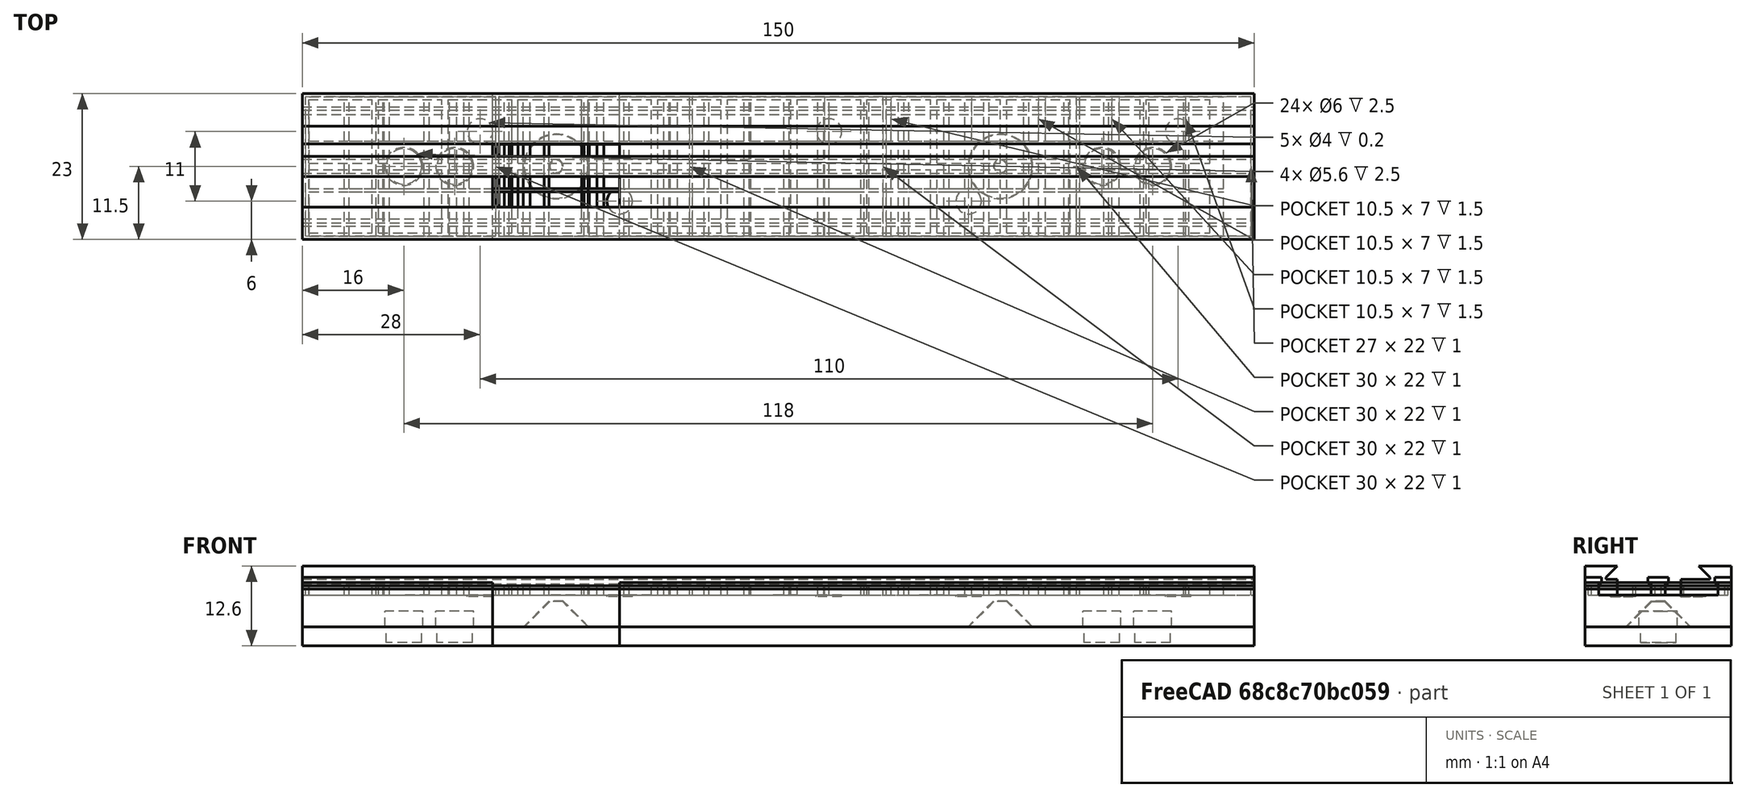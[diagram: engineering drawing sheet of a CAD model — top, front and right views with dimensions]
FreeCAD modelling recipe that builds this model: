
FCSTD DOCUMENT  (FreeCAD 0.19R24366 (Git))
Label: SMD_TRAY_02
License: All rights reserved
LicenseURL: http://en.wikipedia.org/wiki/All_rights_reserved
objects: Part::Box×87, Part::MultiFuse×60, Part::Cylinder×20, Part::Cut×13, Part::Feature×6, Part::Cone×4
note: 190 computed .brp shape members not serialized (recipe doc carries the construction recipe); baked Part::Feature solids carry a one-line shape summary decoded from their .brp

FEATURE [Part::Cone] Cone  label="cone_001"
  Angle = 360
  AttacherType = Attacher::AttachEngine3D
  Height = 4
  Placement = pos=(40,11.5,3) rot=(0,0,1;0rad)
  Radius1 = 5
  Radius2 = 1
FEATURE [Part::Box] Box  label="base"
  AttacherType = Attacher::AttachEngine3D
  Height = 3
  Length = 150
  Width = 23
FEATURE [Part::Cylinder] Cylinder  label="magnet_001"
  Angle = 360
  AttacherType = Attacher::AttachEngine3D
  Height = 2.5
  Placement = pos=(16,11.5,0.5) rot=(0,0,1;0rad)
  Radius = 2.8
FEATURE [Part::Cylinder] Cylinder001  label="magnet_002"
  Angle = 360
  AttacherType = Attacher::AttachEngine3D
  Height = 2.5
  Placement = pos=(24,11.5,0.5) rot=(0,0,1;0rad)
  Radius = 2.8
FEATURE [Part::Cylinder] Cylinder002  label="magnet_003"
  Angle = 360
  AttacherType = Attacher::AttachEngine3D
  Height = 2.5
  Placement = pos=(126,11.5,0.5) rot=(0,0,1;0rad)
  Radius = 2.8
FEATURE [Part::Cylinder] Cylinder003  label="magnet_004"
  Angle = 360
  AttacherType = Attacher::AttachEngine3D
  Height = 2.5
  Placement = pos=(134,11.5,0.5) rot=(0,0,1;0rad)
  Radius = 2.8
FEATURE [Part::Cone] Cone001  label="cone_002"
  Angle = 360
  AttacherType = Attacher::AttachEngine3D
  Height = 4
  Placement = pos=(110,11.5,3) rot=(0,0,1;0rad)
  Radius1 = 5
  Radius2 = 1
FEATURE [Part::MultiFuse] Fusion
  Shapes = -> [Cylinder,Cylinder002,Cylinder001,Cylinder003]
FEATURE [Part::MultiFuse] Fusion001
  Shapes = -> [Cone001,Cone,Box]
FEATURE [Part::Cut] Cut  label="BOTTOM"
  Base = -> Fusion001
  Tool = -> Fusion
FEATURE [Part::Box] Box001  label="Cube"
  AttacherType = Attacher::AttachEngine3D
  Height = 5
  Length = 150
  Placement = pos=(0,0,3) rot=(0,0,1;0rad)
  Width = 23
FEATURE [Part::Cone] Cone002  label="cone_003"
  Angle = 360
  AttacherType = Attacher::AttachEngine3D
  Height = 4.1
  Placement = pos=(40,11.5,3) rot=(0,0,1;0rad)
  Radius1 = 5.1
  Radius2 = 1.1
FEATURE [Part::Cone] Cone003  label="cone_004"
  Angle = 360
  AttacherType = Attacher::AttachEngine3D
  Height = 4.1
  Placement = pos=(110,11.5,3) rot=(0,0,1;0rad)
  Radius1 = 5.1
  Radius2 = 1.1
FEATURE [Part::Cylinder] Cylinder004  label="magnet_005"
  Angle = 360
  AttacherType = Attacher::AttachEngine3D
  Height = 2.5
  Placement = pos=(16,11.5,3) rot=(0,0,1;0rad)
  Radius = 3
FEATURE [Part::Cylinder] Cylinder005  label="magnet_006"
  Angle = 360
  AttacherType = Attacher::AttachEngine3D
  Height = 2.5
  Placement = pos=(126,11.5,3) rot=(0,0,1;0rad)
  Radius = 3
FEATURE [Part::Cylinder] Cylinder006  label="magnet_007"
  Angle = 360
  AttacherType = Attacher::AttachEngine3D
  Height = 2.5
  Placement = pos=(24,11.5,3) rot=(0,0,1;0rad)
  Radius = 3
FEATURE [Part::Cylinder] Cylinder007  label="magnet_008"
  Angle = 360
  AttacherType = Attacher::AttachEngine3D
  Height = 2.5
  Placement = pos=(134,11.5,3) rot=(0,0,1;0rad)
  Radius = 3
FEATURE [Part::MultiFuse] Fusion002  label="removals"
  Shapes = -> [Cylinder004,Cone002,Cone003,Cylinder006,Cylinder005,Cylinder007]
FEATURE [Part::Cut] Cut001  label="TOP"
  Base = -> Box001
  Tool = -> Fusion002
FEATURE [Part::Box] Box014  label="Base002"
  AttacherType = Attacher::AttachEngine3D
  Height = 2.8
  Length = 150
  Placement = pos=(0,0,9) rot=(0,0,1;0rad)
  Width = 23
FEATURE [Part::Box] Box015  label="tape_01"
  AttacherType = Attacher::AttachEngine3D
  Height = 1.8
  Length = 150
  Placement = pos=(0,2.1,9) rot=(0,0,1;0rad)
  Width = 8.3
FEATURE [Part::Box] Box016  label="tape_002"
  AttacherType = Attacher::AttachEngine3D
  Height = 1.8
  Length = 150
  Placement = pos=(0,12.6,9) rot=(0,0,1;0rad)
  Width = 8.3
FEATURE [Part::Box] Box017  label="tape_003"
  AttacherType = Attacher::AttachEngine3D
  Height = 1
  Length = 150
  Placement = pos=(0,2.6,10.8) rot=(0,0,1;0rad)
  Width = 7.3
FEATURE [Part::Box] Box018  label="tape_004"
  AttacherType = Attacher::AttachEngine3D
  Height = 1
  Length = 150
  Placement = pos=(0,13.1,10.8) rot=(0,0,1;0rad)
  Width = 7.3
FEATURE [Part::MultiFuse] Fusion006
  Shapes = -> [Box015,Box017,Box018,Box016]
FEATURE [Part::Cut] Cut006  label="2X_8mm_tape"
  Base = -> Box014
  Placement = pos=(0,0,-1) rot=(0,0,1;0rad)
  Tool = -> Fusion006
FEATURE [Part::Box] Box019  label="deletor_001"
  AttacherType = Attacher::AttachEngine3D
  Height = 10
  Length = 30
  Width = 23
FEATURE [Part::Box] Box020  label="deletor_002"
  AttacherType = Attacher::AttachEngine3D
  Height = 10
  Length = 100
  Placement = pos=(50,0,0) rot=(0,0,1;0rad)
  Width = 23
FEATURE [Part::MultiFuse] Fusion007  label="del_001"
  Shapes = -> [Box019,Box020]
FEATURE [Part::MultiFuse] Fusion008  label="del_002"
  Shapes = -> [Box019,Box020]
FEATURE [Part::MultiFuse] Fusion009  label="TOP_2X_8mm"
  Shapes = -> [Cut001,Cut006]
FEATURE [Part::Cut] Cut007  label="TOP001"
  Base = -> Box001
  Tool = -> Fusion002
FEATURE [Part::Box] Box021  label="Base003"
  AttacherType = Attacher::AttachEngine3D
  Height = 1.5
  Length = 150
  Placement = pos=(0,0,8) rot=(0,0,1;0rad)
  Width = 23
FEATURE [Part::Box] Box022  label="Cube001"
  AttacherType = Attacher::AttachEngine3D
  Height = 1.5
  Length = 5.5
  Placement = pos=(1.1,0.5,8) rot=(0,0,1;0rad)
  Width = 7
FEATURE [Part::Box] Box023  label="Cube002"
  AttacherType = Attacher::AttachEngine3D
  Height = 1.5
  Length = 5.5
  Placement = pos=(1.1,8,8) rot=(0,0,1;0rad)
  Width = 7
FEATURE [Part::Box] Box024  label="Cube003"
  AttacherType = Attacher::AttachEngine3D
  Height = 1.5
  Length = 5.5
  Placement = pos=(1.1,15.5,8) rot=(0,0,1;0rad)
  Width = 7
FEATURE [Part::MultiFuse] Fusion010  label="row_000"
  Shapes = -> [Box022,Box024,Box023]
FEATURE [Part::MultiFuse] Fusion011  label="row_001"
  Placement = pos=(6.3,0,0) rot=(0,0,1;0rad)
  Shapes = -> [Box022,Box024,Box023]
FEATURE [Part::MultiFuse] Fusion012  label="row_002"
  Placement = pos=(12.6,0,0) rot=(0,0,1;0rad)
  Shapes = -> [Box022,Box024,Box023]
FEATURE [Part::MultiFuse] Fusion013  label="row_003"
  Placement = pos=(18.9,0,0) rot=(0,0,1;0rad)
  Shapes = -> [Box022,Box024,Box023]
FEATURE [Part::MultiFuse] Fusion014  label="row_004"
  Placement = pos=(25.2,0,0) rot=(0,0,1;0rad)
  Shapes = -> [Box022,Box024,Box023]
FEATURE [Part::MultiFuse] Fusion015  label="row_005"
  Placement = pos=(31.5,0,0) rot=(0,0,1;0rad)
  Shapes = -> [Box022,Box024,Box023]
FEATURE [Part::MultiFuse] Fusion016  label="row_006"
  Placement = pos=(37.8,0,0) rot=(0,0,1;0rad)
  Shapes = -> [Box022,Box024,Box023]
FEATURE [Part::MultiFuse] Fusion017  label="row_007"
  Placement = pos=(44.1,0,0) rot=(0,0,1;0rad)
  Shapes = -> [Box022,Box024,Box023]
FEATURE [Part::MultiFuse] Fusion018  label="row_008"
  Placement = pos=(50.4,0,0) rot=(0,0,1;0rad)
  Shapes = -> [Box022,Box024,Box023]
FEATURE [Part::MultiFuse] Fusion019  label="row_009"
  Placement = pos=(56.7,0,0) rot=(0,0,1;0rad)
  Shapes = -> [Box022,Box024,Box023]
FEATURE [Part::MultiFuse] Fusion020  label="10 of them"
  Shapes = -> [Fusion010,Fusion019,Fusion018,Fusion014,Fusion015,Fusion017,Fusion016,Fusion013,Fusion011,Fusion012]
FEATURE [Part::MultiFuse] Fusion021  label="10 of them001"
  Placement = pos=(63,0,0) rot=(0,0,1;0rad)
  Shapes = -> [Fusion010,Fusion019,Fusion018,Fusion014,Fusion015,Fusion017,Fusion016,Fusion013,Fusion011,Fusion012]
FEATURE [Part::MultiFuse] Fusion022  label="row_010"
  Placement = pos=(126,0,0) rot=(0,0,1;0rad)
  Shapes = -> [Box022,Box024,Box023]
FEATURE [Part::MultiFuse] Fusion023  label="row_011"
  Placement = pos=(132.3,0,0) rot=(0,0,1;0rad)
  Shapes = -> [Box022,Box024,Box023]
FEATURE [Part::MultiFuse] Fusion024  label="row_012"
  Placement = pos=(138.6,0,0) rot=(0,0,1;0rad)
  Shapes = -> [Box022,Box024,Box023]
FEATURE [Part::MultiFuse] Fusion025  label="Holes_SOIC8"
  Shapes = -> [Fusion020,Fusion021,Fusion022,Fusion024,Fusion023]
FEATURE [Part::Cut] Cut008  label="69X_SOIC8"
  Base = -> Box021
  Tool = -> Fusion025
FEATURE [Part::MultiFuse] Fusion026  label="TOP_69X_SOIC8"
  Shapes = -> [Cut007,Cut008]
FEATURE [Part::Cut] Cut009  label="TOP002"
  Base = -> Box001
  Tool = -> Fusion002
FEATURE [Part::Box] Box025  label="Base004"
  AttacherType = Attacher::AttachEngine3D
  Height = 1
  Length = 150
  Placement = pos=(0,0,8) rot=(0,0,1;0rad)
  Width = 23
FEATURE [Part::Box] Box026  label="Cube004"
  AttacherType = Attacher::AttachEngine3D
  Height = 1.5
  Length = 30
  Placement = pos=(0.5,0.5,8) rot=(0,0,1;0rad)
  Width = 22
FEATURE [Part::Box] Box027  label="Cube005"
  AttacherType = Attacher::AttachEngine3D
  Height = 1.5
  Length = 30
  Placement = pos=(31,0.5,8) rot=(0,0,1;0rad)
  Width = 22
FEATURE [Part::Box] Box028  label="Cube006"
  AttacherType = Attacher::AttachEngine3D
  Height = 1.5
  Length = 30
  Placement = pos=(61.5,0.5,8) rot=(0,0,1;0rad)
  Width = 22
FEATURE [Part::Box] Box029  label="Cube007"
  AttacherType = Attacher::AttachEngine3D
  Height = 1.5
  Length = 30
  Placement = pos=(92,0.5,8) rot=(0,0,1;0rad)
  Width = 22
FEATURE [Part::Box] Box030  label="Cube008"
  AttacherType = Attacher::AttachEngine3D
  Height = 1.5
  Length = 27
  Placement = pos=(122.5,0.5,8) rot=(0,0,1;0rad)
  Width = 22
FEATURE [Part::MultiFuse] Fusion027  label="remove_holes"
  Shapes = -> [Box026,Box029,Box030,Box028,Box027]
FEATURE [Part::Cut] Cut010  label="5x_loose"
  Base = -> Box025
  Tool = -> Fusion027
FEATURE [Part::MultiFuse] Fusion028  label="TOP_5X_Loose"
  Shapes = -> [Cut009,Cut010]
FEATURE [Part::Feature] Cut007001  label="TOP003"
  shape: bbox 150 x 23 x 5 mm, 18 faces (baked)
FEATURE [Part::Feature] Box021001  label="Base005"
  Placement = pos=(0,0,8) rot=(0,0,1;0rad)
  shape: bbox 150 x 23 x 1.5 mm, 6 faces (baked)
FEATURE [Part::Box] Box021002  label="Cube009"
  AttacherType = Attacher::AttachEngine3D
  Height = 1.5
  Length = 10.5
  Placement = pos=(1.1,0.5,8) rot=(0,0,1;0rad)
  Width = 7
FEATURE [Part::Box] Box021003  label="Cube010"
  AttacherType = Attacher::AttachEngine3D
  Height = 1.5
  Length = 10.5
  Placement = pos=(1.1,8,8) rot=(0,0,1;0rad)
  Width = 7
FEATURE [Part::Box] Box021004  label="Cube011"
  AttacherType = Attacher::AttachEngine3D
  Height = 1.5
  Length = 10.5
  Placement = pos=(1.1,15.5,8) rot=(0,0,1;0rad)
  Width = 7
FEATURE [Part::MultiFuse] Fusion029  label="row__01"
  Shapes = -> [Box021002,Box021003,Box021004]
FEATURE [Part::Box] Box021005  label="Cube012"
  AttacherType = Attacher::AttachEngine3D
  Height = 1.5
  Length = 10.5
  Placement = pos=(1.1,8,8) rot=(0,0,1;0rad)
  Width = 7
FEATURE [Part::Box] Box021006  label="Cube013"
  AttacherType = Attacher::AttachEngine3D
  Height = 1.5
  Length = 10.5
  Placement = pos=(1.1,15.5,8) rot=(0,0,1;0rad)
  Width = 7
FEATURE [Part::Box] Box021007  label="Cube014"
  AttacherType = Attacher::AttachEngine3D
  Height = 1.5
  Length = 10.5
  Placement = pos=(1.1,0.5,8) rot=(0,0,1;0rad)
  Width = 7
FEATURE [Part::MultiFuse] Fusion030  label="row__002"
  Placement = pos=(11.6,0,0) rot=(0,0,1;0rad)
  Shapes = -> [Box021007,Box021005,Box021006]
FEATURE [Part::Box] Box021008  label="Cube015"
  AttacherType = Attacher::AttachEngine3D
  Height = 1.5
  Length = 10.5
  Placement = pos=(1.1,0.5,8) rot=(0,0,1;0rad)
  Width = 7
FEATURE [Part::Box] Box021009  label="Cube016"
  AttacherType = Attacher::AttachEngine3D
  Height = 1.5
  Length = 10.5
  Placement = pos=(1.1,8,8) rot=(0,0,1;0rad)
  Width = 7
FEATURE [Part::Box] Box021010  label="Cube017"
  AttacherType = Attacher::AttachEngine3D
  Height = 1.5
  Length = 10.5
  Placement = pos=(1.1,15.5,8) rot=(0,0,1;0rad)
  Width = 7
FEATURE [Part::MultiFuse] Fusion031  label="row__003"
  Placement = pos=(23.2,0,0) rot=(0,0,1;0rad)
  Shapes = -> [Box021008,Box021009,Box021010]
FEATURE [Part::Box] Box021011  label="Cube018"
  AttacherType = Attacher::AttachEngine3D
  Height = 1.5
  Length = 10.5
  Placement = pos=(1.1,0.5,8) rot=(0,0,1;0rad)
  Width = 7
FEATURE [Part::Box] Box021012  label="Cube019"
  AttacherType = Attacher::AttachEngine3D
  Height = 1.5
  Length = 10.5
  Placement = pos=(1.1,8,8) rot=(0,0,1;0rad)
  Width = 7
FEATURE [Part::Box] Box021013  label="Cube020"
  AttacherType = Attacher::AttachEngine3D
  Height = 1.5
  Length = 10.5
  Placement = pos=(1.1,15.5,8) rot=(0,0,1;0rad)
  Width = 7
FEATURE [Part::MultiFuse] Fusion032  label="row__004"
  Placement = pos=(34.8,0,0) rot=(0,0,1;0rad)
  Shapes = -> [Box021011,Box021012,Box021013]
FEATURE [Part::Box] Box021014  label="Cube021"
  AttacherType = Attacher::AttachEngine3D
  Height = 1.5
  Length = 10.5
  Placement = pos=(1.1,0.5,8) rot=(0,0,1;0rad)
  Width = 7
FEATURE [Part::Box] Box021015  label="Cube022"
  AttacherType = Attacher::AttachEngine3D
  Height = 1.5
  Length = 10.5
  Placement = pos=(1.1,8,8) rot=(0,0,1;0rad)
  Width = 7
FEATURE [Part::Box] Box021016  label="Cube023"
  AttacherType = Attacher::AttachEngine3D
  Height = 1.5
  Length = 10.5
  Placement = pos=(1.1,15.5,8) rot=(0,0,1;0rad)
  Width = 7
FEATURE [Part::MultiFuse] Fusion033  label="row__005"
  Placement = pos=(46.4,0,0) rot=(0,0,1;0rad)
  Shapes = -> [Box021014,Box021015,Box021016]
FEATURE [Part::Box] Box021017  label="Cube024"
  AttacherType = Attacher::AttachEngine3D
  Height = 1.5
  Length = 10.5
  Placement = pos=(1.1,0.5,8) rot=(0,0,1;0rad)
  Width = 7
FEATURE [Part::Box] Box021018  label="Cube025"
  AttacherType = Attacher::AttachEngine3D
  Height = 1.5
  Length = 10.5
  Placement = pos=(1.1,8,8) rot=(0,0,1;0rad)
  Width = 7
FEATURE [Part::Box] Box021019  label="Cube026"
  AttacherType = Attacher::AttachEngine3D
  Height = 1.5
  Length = 10.5
  Placement = pos=(1.1,15.5,8) rot=(0,0,1;0rad)
  Width = 7
FEATURE [Part::MultiFuse] Fusion034  label="row__006"
  Placement = pos=(58,0,0) rot=(0,0,1;0rad)
  Shapes = -> [Box021017,Box021018,Box021019]
FEATURE [Part::Box] Box021020  label="Cube027"
  AttacherType = Attacher::AttachEngine3D
  Height = 1.5
  Length = 10.5
  Placement = pos=(1.1,0.5,8) rot=(0,0,1;0rad)
  Width = 7
FEATURE [Part::Box] Box021021  label="Cube028"
  AttacherType = Attacher::AttachEngine3D
  Height = 1.5
  Length = 10.5
  Placement = pos=(1.1,8,8) rot=(0,0,1;0rad)
  Width = 7
FEATURE [Part::Box] Box021022  label="Cube029"
  AttacherType = Attacher::AttachEngine3D
  Height = 1.5
  Length = 10.5
  Placement = pos=(1.1,15.5,8) rot=(0,0,1;0rad)
  Width = 7
FEATURE [Part::MultiFuse] Fusion035  label="row__007"
  Placement = pos=(69.6,0,0) rot=(0,0,1;0rad)
  Shapes = -> [Box021020,Box021021,Box021022]
FEATURE [Part::Box] Box021023  label="Cube030"
  AttacherType = Attacher::AttachEngine3D
  Height = 1.5
  Length = 10.5
  Placement = pos=(1.1,0.5,8) rot=(0,0,1;0rad)
  Width = 7
FEATURE [Part::Box] Box021024  label="Cube031"
  AttacherType = Attacher::AttachEngine3D
  Height = 1.5
  Length = 10.5
  Placement = pos=(1.1,8,8) rot=(0,0,1;0rad)
  Width = 7
FEATURE [Part::Box] Box021025  label="Cube032"
  AttacherType = Attacher::AttachEngine3D
  Height = 1.5
  Length = 10.5
  Placement = pos=(1.1,15.5,8) rot=(0,0,1;0rad)
  Width = 7
FEATURE [Part::MultiFuse] Fusion036  label="row__008"
  Placement = pos=(81.2,0,0) rot=(0,0,1;0rad)
  Shapes = -> [Box021023,Box021024,Box021025]
FEATURE [Part::Box] Box021026  label="Cube033"
  AttacherType = Attacher::AttachEngine3D
  Height = 1.5
  Length = 10.5
  Placement = pos=(1.1,0.5,8) rot=(0,0,1;0rad)
  Width = 7
FEATURE [Part::Box] Box021027  label="Cube034"
  AttacherType = Attacher::AttachEngine3D
  Height = 1.5
  Length = 10.5
  Placement = pos=(1.1,8,8) rot=(0,0,1;0rad)
  Width = 7
FEATURE [Part::Box] Box021028  label="Cube035"
  AttacherType = Attacher::AttachEngine3D
  Height = 1.5
  Length = 10.5
  Placement = pos=(1.1,15.5,8) rot=(0,0,1;0rad)
  Width = 7
FEATURE [Part::MultiFuse] Fusion037  label="row__009"
  Placement = pos=(92.8,0,0) rot=(0,0,1;0rad)
  Shapes = -> [Box021026,Box021027,Box021028]
FEATURE [Part::Box] Box021029  label="Cube036"
  AttacherType = Attacher::AttachEngine3D
  Height = 1.5
  Length = 10.5
  Placement = pos=(1.1,0.5,8) rot=(0,0,1;0rad)
  Width = 7
FEATURE [Part::Box] Box021030  label="Cube037"
  AttacherType = Attacher::AttachEngine3D
  Height = 1.5
  Length = 10.5
  Placement = pos=(1.1,8,8) rot=(0,0,1;0rad)
  Width = 7
FEATURE [Part::Box] Box021031  label="Cube038"
  AttacherType = Attacher::AttachEngine3D
  Height = 1.5
  Length = 10.5
  Placement = pos=(1.1,15.5,8) rot=(0,0,1;0rad)
  Width = 7
FEATURE [Part::MultiFuse] Fusion038  label="row__010"
  Placement = pos=(104.4,0,0) rot=(0,0,1;0rad)
  Shapes = -> [Box021029,Box021030,Box021031]
FEATURE [Part::Box] Box021032  label="Cube039"
  AttacherType = Attacher::AttachEngine3D
  Height = 1.5
  Length = 10.5
  Placement = pos=(1.1,0.5,8) rot=(0,0,1;0rad)
  Width = 7
FEATURE [Part::Box] Box021033  label="Cube040"
  AttacherType = Attacher::AttachEngine3D
  Height = 1.5
  Length = 10.5
  Placement = pos=(1.1,8,8) rot=(0,0,1;0rad)
  Width = 7
FEATURE [Part::Box] Box021034  label="Cube041"
  AttacherType = Attacher::AttachEngine3D
  Height = 1.5
  Length = 10.5
  Placement = pos=(1.1,15.5,8) rot=(0,0,1;0rad)
  Width = 7
FEATURE [Part::MultiFuse] Fusion039  label="row__011"
  Placement = pos=(116,0,0) rot=(0,0,1;0rad)
  Shapes = -> [Box021032,Box021033,Box021034]
FEATURE [Part::Box] Box021035  label="Cube042"
  AttacherType = Attacher::AttachEngine3D
  Height = 1.5
  Length = 10.5
  Placement = pos=(1.1,0.5,8) rot=(0,0,1;0rad)
  Width = 7
FEATURE [Part::Box] Box021036  label="Cube043"
  AttacherType = Attacher::AttachEngine3D
  Height = 1.5
  Length = 10.5
  Placement = pos=(1.1,8,8) rot=(0,0,1;0rad)
  Width = 7
FEATURE [Part::Box] Box021037  label="Cube044"
  AttacherType = Attacher::AttachEngine3D
  Height = 1.5
  Length = 10.5
  Placement = pos=(1.1,15.5,8) rot=(0,0,1;0rad)
  Width = 7
FEATURE [Part::MultiFuse] Fusion040  label="row__012"
  Placement = pos=(127.6,0,0) rot=(0,0,1;0rad)
  Shapes = -> [Box021035,Box021036,Box021037]
FEATURE [Part::Cylinder] Cylinder008  label="mark_5"
  Angle = 360
  AttacherType = Attacher::AttachEngine3D
  Height = 0.2
  Placement = pos=(18,12,8) rot=(0,0,1;0rad)
  Radius = 2
FEATURE [Part::Cylinder] Cylinder009  label="mark_10"
  Angle = 360
  AttacherType = Attacher::AttachEngine3D
  Height = 0.2
  Placement = pos=(41,19,8) rot=(0,0,1;0rad)
  Radius = 2
FEATURE [Part::Cylinder] Cylinder010  label="mark_15"
  Angle = 360
  AttacherType = Attacher::AttachEngine3D
  Height = 0.2
  Placement = pos=(53,4,8) rot=(0,0,1;0rad)
  Radius = 2
FEATURE [Part::Cylinder] Cylinder011  label="mark_20"
  Angle = 360
  AttacherType = Attacher::AttachEngine3D
  Height = 0.2
  Placement = pos=(76,12,8) rot=(0,0,1;0rad)
  Radius = 2
FEATURE [Part::Cylinder] Cylinder012  label="mark_25"
  Angle = 360
  AttacherType = Attacher::AttachEngine3D
  Height = 0.2
  Placement = pos=(99,19,8) rot=(0,0,1;0rad)
  Radius = 2
FEATURE [Part::Cylinder] Cylinder013  label="mark_30"
  Angle = 360
  AttacherType = Attacher::AttachEngine3D
  Height = 0.2
  Placement = pos=(111,4,8) rot=(0,0,1;0rad)
  Radius = 2
FEATURE [Part::Cylinder] Cylinder014  label="mark_35"
  Angle = 360
  AttacherType = Attacher::AttachEngine3D
  Height = 0.2
  Placement = pos=(134,12,8) rot=(0,0,1;0rad)
  Radius = 2
FEATURE [Part::MultiFuse] Fusion041
  Shapes = -> [Fusion029,Fusion030,Fusion031,Fusion032,Fusion033,Fusion034,Fusion035,Fusion036,Fusion037,Fusion038,Fusion039,Fusion040]
FEATURE [Part::MultiFuse] Fusion042
  Shapes = -> [Cylinder008,Cylinder009,Cylinder010,Cylinder011,Cylinder012,Cylinder013,Cylinder014]
FEATURE [Part::MultiFuse] Fusion043
  Shapes = -> [Cut007001,Box021001]
FEATURE [Part::Cut] Cut007002
  Base = -> Fusion043
  Tool = -> Fusion042
FEATURE [Part::Cut] Cut007003  label="TOP_36X_SOIC16"
  Base = -> Cut007002
  Tool = -> Fusion041
FEATURE [Part::Feature] Box021038  label="Base006"
  Placement = pos=(0,0,8) rot=(0,0,1;0rad)
  shape: bbox 150 x 23 x 1.5 mm, 6 faces (baked)
FEATURE [Part::Feature] Cut007004  label="TOP004"
  shape: bbox 150 x 23 x 5 mm, 18 faces (baked)
FEATURE [Part::Box] Box021039  label="Cube045"
  AttacherType = Attacher::AttachEngine3D
  Height = 1.5
  Length = 10
  Placement = pos=(1,1,8) rot=(0,0,1;0rad)
  Width = 10
FEATURE [Part::Box] Box021040  label="Cube046"
  AttacherType = Attacher::AttachEngine3D
  Height = 1.5
  Length = 10
  Placement = pos=(1,12,8) rot=(0,0,1;0rad)
  Width = 10
FEATURE [Part::MultiFuse] Fusion044
  Shapes = -> [Box021039,Box021040]
FEATURE [Part::Box] Box021041  label="Cube047"
  AttacherType = Attacher::AttachEngine3D
  Height = 1.5
  Length = 10
  Placement = pos=(1,12,8) rot=(0,0,1;0rad)
  Width = 10
FEATURE [Part::Box] Box021042  label="Cube048"
  AttacherType = Attacher::AttachEngine3D
  Height = 1.5
  Length = 10
  Placement = pos=(1,1,8) rot=(0,0,1;0rad)
  Width = 10
FEATURE [Part::MultiFuse] Fusion045
  Placement = pos=(11,0,0) rot=(0,0,1;0rad)
  Shapes = -> [Box021042,Box021041]
FEATURE [Part::Box] Box021043  label="Cube049"
  AttacherType = Attacher::AttachEngine3D
  Height = 1.5
  Length = 10
  Placement = pos=(1,12,8) rot=(0,0,1;0rad)
  Width = 10
FEATURE [Part::Box] Box021044  label="Cube050"
  AttacherType = Attacher::AttachEngine3D
  Height = 1.5
  Length = 10
  Placement = pos=(1,1,8) rot=(0,0,1;0rad)
  Width = 10
FEATURE [Part::MultiFuse] Fusion046
  Placement = pos=(22,0,0) rot=(0,0,1;0rad)
  Shapes = -> [Box021044,Box021043]
FEATURE [Part::Box] Box021045  label="Cube051"
  AttacherType = Attacher::AttachEngine3D
  Height = 1.5
  Length = 10
  Placement = pos=(1,12,8) rot=(0,0,1;0rad)
  Width = 10
FEATURE [Part::Box] Box021046  label="Cube052"
  AttacherType = Attacher::AttachEngine3D
  Height = 1.5
  Length = 10
  Placement = pos=(1,1,8) rot=(0,0,1;0rad)
  Width = 10
FEATURE [Part::MultiFuse] Fusion047
  Placement = pos=(33,0,0) rot=(0,0,1;0rad)
  Shapes = -> [Box021046,Box021045]
FEATURE [Part::Box] Box021047  label="Cube053"
  AttacherType = Attacher::AttachEngine3D
  Height = 1.5
  Length = 10
  Placement = pos=(1,12,8) rot=(0,0,1;0rad)
  Width = 10
FEATURE [Part::Box] Box021048  label="Cube054"
  AttacherType = Attacher::AttachEngine3D
  Height = 1.5
  Length = 10
  Placement = pos=(1,1,8) rot=(0,0,1;0rad)
  Width = 10
FEATURE [Part::MultiFuse] Fusion048
  Placement = pos=(44,0,0) rot=(0,0,1;0rad)
  Shapes = -> [Box021048,Box021047]
FEATURE [Part::Box] Box021049  label="Cube055"
  AttacherType = Attacher::AttachEngine3D
  Height = 1.5
  Length = 10
  Placement = pos=(1,12,8) rot=(0,0,1;0rad)
  Width = 10
FEATURE [Part::Box] Box021050  label="Cube056"
  AttacherType = Attacher::AttachEngine3D
  Height = 1.5
  Length = 10
  Placement = pos=(1,1,8) rot=(0,0,1;0rad)
  Width = 10
FEATURE [Part::MultiFuse] Fusion049
  Placement = pos=(55,0,0) rot=(0,0,1;0rad)
  Shapes = -> [Box021050,Box021049]
FEATURE [Part::Box] Box021051  label="Cube057"
  AttacherType = Attacher::AttachEngine3D
  Height = 1.5
  Length = 10
  Placement = pos=(1,12,8) rot=(0,0,1;0rad)
  Width = 10
FEATURE [Part::Box] Box021052  label="Cube058"
  AttacherType = Attacher::AttachEngine3D
  Height = 1.5
  Length = 10
  Placement = pos=(1,1,8) rot=(0,0,1;0rad)
  Width = 10
FEATURE [Part::MultiFuse] Fusion050
  Placement = pos=(66,0,0) rot=(0,0,1;0rad)
  Shapes = -> [Box021052,Box021051]
FEATURE [Part::Box] Box021053  label="Cube059"
  AttacherType = Attacher::AttachEngine3D
  Height = 1.5
  Length = 10
  Placement = pos=(1,12,8) rot=(0,0,1;0rad)
  Width = 10
FEATURE [Part::Box] Box021054  label="Cube060"
  AttacherType = Attacher::AttachEngine3D
  Height = 1.5
  Length = 10
  Placement = pos=(1,1,8) rot=(0,0,1;0rad)
  Width = 10
FEATURE [Part::MultiFuse] Fusion051
  Placement = pos=(77,0,0) rot=(0,0,1;0rad)
  Shapes = -> [Box021054,Box021053]
FEATURE [Part::Box] Box021055  label="Cube061"
  AttacherType = Attacher::AttachEngine3D
  Height = 1.5
  Length = 10
  Placement = pos=(1,12,8) rot=(0,0,1;0rad)
  Width = 10
FEATURE [Part::Box] Box021056  label="Cube062"
  AttacherType = Attacher::AttachEngine3D
  Height = 1.5
  Length = 10
  Placement = pos=(1,1,8) rot=(0,0,1;0rad)
  Width = 10
FEATURE [Part::MultiFuse] Fusion052
  Placement = pos=(88,0,0) rot=(0,0,1;0rad)
  Shapes = -> [Box021056,Box021055]
FEATURE [Part::Box] Box021057  label="Cube063"
  AttacherType = Attacher::AttachEngine3D
  Height = 1.5
  Length = 10
  Placement = pos=(1,12,8) rot=(0,0,1;0rad)
  Width = 10
FEATURE [Part::Box] Box021058  label="Cube064"
  AttacherType = Attacher::AttachEngine3D
  Height = 1.5
  Length = 10
  Placement = pos=(1,1,8) rot=(0,0,1;0rad)
  Width = 10
FEATURE [Part::MultiFuse] Fusion053
  Placement = pos=(99,0,0) rot=(0,0,1;0rad)
  Shapes = -> [Box021058,Box021057]
FEATURE [Part::Box] Box021059  label="Cube065"
  AttacherType = Attacher::AttachEngine3D
  Height = 1.5
  Length = 10
  Placement = pos=(1,12,8) rot=(0,0,1;0rad)
  Width = 10
FEATURE [Part::Box] Box021060  label="Cube066"
  AttacherType = Attacher::AttachEngine3D
  Height = 1.5
  Length = 10
  Placement = pos=(1,1,8) rot=(0,0,1;0rad)
  Width = 10
FEATURE [Part::MultiFuse] Fusion054
  Placement = pos=(110,0,0) rot=(0,0,1;0rad)
  Shapes = -> [Box021060,Box021059]
FEATURE [Part::Box] Box021061  label="Cube067"
  AttacherType = Attacher::AttachEngine3D
  Height = 1.5
  Length = 10
  Placement = pos=(1,12,8) rot=(0,0,1;0rad)
  Width = 10
FEATURE [Part::Box] Box021062  label="Cube068"
  AttacherType = Attacher::AttachEngine3D
  Height = 1.5
  Length = 10
  Placement = pos=(1,1,8) rot=(0,0,1;0rad)
  Width = 10
FEATURE [Part::MultiFuse] Fusion055
  Placement = pos=(121,0,0) rot=(0,0,1;0rad)
  Shapes = -> [Box021062,Box021061]
FEATURE [Part::Box] Box021063  label="Cube069"
  AttacherType = Attacher::AttachEngine3D
  Height = 1.5
  Length = 10
  Placement = pos=(1,12,8) rot=(0,0,1;0rad)
  Width = 10
FEATURE [Part::Box] Box021064  label="Cube070"
  AttacherType = Attacher::AttachEngine3D
  Height = 1.5
  Length = 10
  Placement = pos=(1,1,8) rot=(0,0,1;0rad)
  Width = 10
FEATURE [Part::MultiFuse] Fusion056
  Placement = pos=(132,0,0) rot=(0,0,1;0rad)
  Shapes = -> [Box021064,Box021063]
FEATURE [Part::Cylinder] Cylinder015  label="mark_036"
  Angle = 360
  AttacherType = Attacher::AttachEngine3D
  Height = 0.2
  Placement = pos=(28,17,7.8) rot=(0,0,1;0rad)
  Radius = 2
FEATURE [Part::MultiFuse] Fusion057
  Shapes = -> [Fusion056,Fusion044,Fusion045,Fusion046,Fusion047,Fusion048,Fusion049,Fusion050,Fusion051,Fusion052,Fusion053,Fusion054,Fusion055]
FEATURE [Part::Cut] Cut007005
  Base = -> Box021038
  Tool = -> Fusion057
FEATURE [Part::MultiFuse] Fusion058
  Shapes = -> [Cut007005,Cut007004]
FEATURE [Part::Cylinder] Cylinder016  label="mark_037"
  Angle = 360
  AttacherType = Attacher::AttachEngine3D
  Height = 0.2
  Placement = pos=(50,6,7.8) rot=(0,0,1;0rad)
  Radius = 2
FEATURE [Part::Cylinder] Cylinder017  label="mark_038"
  Angle = 360
  AttacherType = Attacher::AttachEngine3D
  Height = 0.2
  Placement = pos=(83,17,7.8) rot=(0,0,1;0rad)
  Radius = 2
FEATURE [Part::Cylinder] Cylinder018  label="mark_039"
  Angle = 360
  AttacherType = Attacher::AttachEngine3D
  Height = 0.2
  Placement = pos=(105,6,7.8) rot=(0,0,1;0rad)
  Radius = 2
FEATURE [Part::Cylinder] Cylinder019  label="mark_040"
  Angle = 360
  AttacherType = Attacher::AttachEngine3D
  Height = 0.2
  Placement = pos=(138,17,7.8) rot=(0,0,1;0rad)
  Radius = 2
FEATURE [Part::MultiFuse] Fusion059
  Shapes = -> [Cylinder015,Cylinder016,Cylinder017,Cylinder018,Cylinder019]
FEATURE [Part::Cut] Cut007006  label="TOP_26X_TQFP32"
  Base = -> Fusion058
  Tool = -> Fusion059
FEATURE [Part::Feature] Cut007007  label="BOTTOM001"
  shape: bbox 150 x 23 x 7 mm, 18 faces (baked)
FEATURE [Part::Feature] Cut007008  label="TOP005"
  shape: bbox 150 x 23 x 5 mm, 18 faces (baked)
FEATURE [Part::Box] Box021065  label="cube_bizeau_002"
  AttacherType = Attacher::AttachEngine3D
  Height = 160
  Length = 5
  Placement = pos=(15,7.05,0) rot=(0,0,-1;0.785398rad)
  Width = 3
FEATURE [Part::Box] Box021066  label="Cube071"
  AttacherType = Attacher::AttachEngine3D
  Height = 160
  Length = 16.4
  Placement = pos=(1.15,4.2,0) rot=(0,0,1;0rad)
  Width = 0.3
FEATURE [Part::Box] Box021067  label="Cube072"
  AttacherType = Attacher::AttachEngine3D
  Height = 160
  Length = 16.4
  Placement = pos=(1.15,4.5,0) rot=(0,0,1;0rad)
  Width = 1.8
FEATURE [Part::Box] Box033  label="Cube073"
  AttacherType = Attacher::AttachEngine3D
  Height = 160
  Length = 10
  Placement = pos=(2.95,1.7,0) rot=(0,0,1;0rad)
  Width = 2.5
FEATURE [Part::Box] Box021068  label="cube_bizeau_01"
  AttacherType = Attacher::AttachEngine3D
  Height = 160
  Length = 5
  Placement = pos=(0,3.35,0) rot=(0,0,1;0.785398rad)
  Width = 3
FEATURE [Part::MultiFuse] Fusion003006
  Shapes = -> [Box021068,Box021065]
FEATURE [Part::Cut] Cut002
  Base = -> Box021067
  Tool = -> Fusion003006
FEATURE [Part::MultiFuse] Fusion003005
  Placement = pos=(5e-16,2.1,6.3) rot=(0.57735,0.57735,0.57735;2.0944rad)
  Shapes = -> [Box033,Cut002,Box021066]
FEATURE [Part::Box] Box021069  label="Cube074"
  AttacherType = Attacher::AttachEngine3D
  Height = 4.6
  Length = 150
  Placement = pos=(0,0,8) rot=(0,0,1;0rad)
  Width = 23
FEATURE [Part::MultiFuse] Fusion003007
  Shapes = -> [Cut007008,Box021069]
FEATURE [Part::Cut] Cut007009  label="TOP_1X_16mm"
  Base = -> Fusion003007
  Tool = -> Fusion003005
